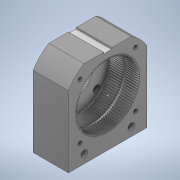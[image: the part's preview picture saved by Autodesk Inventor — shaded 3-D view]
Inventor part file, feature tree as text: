
AUTODESK INVENTOR PART (.ipt)
format: ipt  version: 2022 (Build 260153000, 153)  size: 1,537,536 bytes
history: mixed  units: mm
features: sketch x6, extrude x5, other x3, fillet x1, imported_body x1
ambient origin geometry x8: Origin, YZ Plane, XZ Plane, XY Plane, X Axis, Y Axis, Z Axis, Center Point
bodies: Solid1 (imported_parasolid)
feature tree (16):
  other  "Assembly2.iam"
  other  "96Gears_Stage_1_modified.ipt:1"
  other  "96Gears_Stage_2_modified.ipt:1"
  extrude  "Extrusion3"  Depth=3.0mm
  extrude  "Extrusion5"  Depth=1.0mm TaperAngle=0.0deg
  extrude  "Extrusion6"  Depth=6.0mm TaperAngle=0.0deg
  extrude  "Extrusion7"  TaperAngle=0.0deg  [1 undecoded]
  extrude  "Extrusion8"  Depth=3.5mm
  fillet  "Fillet1"  [1 undecoded]
  sketch  "Sketch5"  dims[d7=6.0mm d8=1.0mm d9=0.0mm]
  sketch  "Sketch4"  dims[d0=10.0mm d6=3.0mm]
  sketch  "Sketch7"  dims[d17=32.25mm d18=6.0mm d19=0.0mm]
  sketch  "Sketch8"  dims[d20=10.0mm d21=0.0mm d22=0.0mm]
  sketch  "Sketch9"  dims[d23=6.75mm d27=3.5mm d28=0.0mm d29=0.0mm]
  sketch  "Sketch10"  dims[d30=5.0mm d31=3.0mm d32=0.0mm d33=1.0mm]
  imported_body  NMx_Import_Brep_tag  [imported B-rep: ~819 faces, bbox_mm=[27.0, 66.5, 60.0]]
note: 2 required parameter values undecoded (feature->parameter linkage not recoverable at this tier; creation-order binding heuristic only, values carry confidence <= 0.55)
